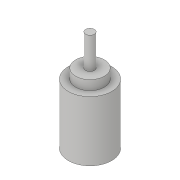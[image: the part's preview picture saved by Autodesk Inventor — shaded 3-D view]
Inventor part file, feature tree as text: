
AUTODESK INVENTOR PART (.ipt)
format: ipt  version: 2019 (Build 230136000, 136)  size: 88,576 bytes
history: native  units: in
note: dims shown in document units (in); Inventor stores cm internally (conversion verified against a paired STEP export)
features: sketch x4, extrude x3
ambient origin geometry x8: Origin, YZ Plane, XZ Plane, XY Plane, X Axis, Y Axis, Z Axis, Center Point
bodies: Solid1 (feature_tree)
feature tree (7):
  extrude  "Extrusion1"  Depth=1.7323in
  extrude  "Extrusion2"  Depth=0.9055in TaperAngle=0.0deg
  extrude  "Extrusion3"  [1 undecoded]
  sketch  "Sketch4"
  sketch  "Sketch1"  dims[d0=1.7323in d1=0.0in d2=0.8268in]
  sketch  "Sketch2"  dims[d3=0.2756in d4=0.0in d5=0.9055in d6=0.0in]
  sketch  "Sketch3"
note: 1 required parameter value undecoded (feature->parameter linkage not recoverable at this tier; creation-order binding heuristic only, values carry confidence <= 0.55)
